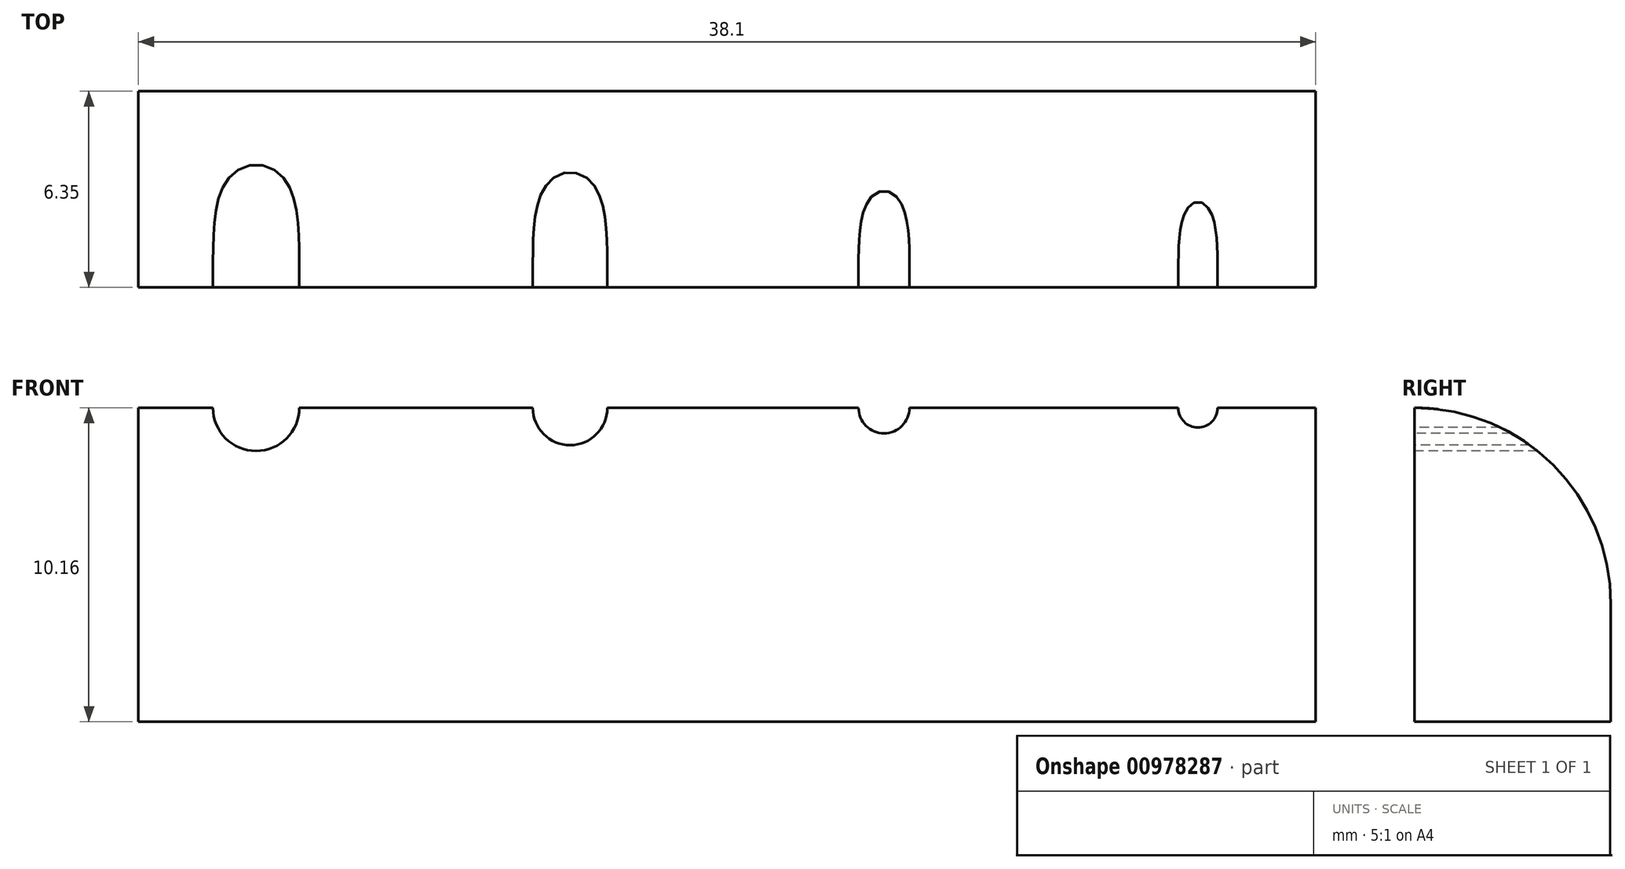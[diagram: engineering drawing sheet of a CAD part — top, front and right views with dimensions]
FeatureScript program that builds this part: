
annotation { "Feature Type Name" : "Feature", "Feature Type Description" : "" }
export const myFeature = defineFeature(function(context is Context, id is Id, definition is map)
    precondition{}
    {
        {
            var Q0;
            Q0=qCreatedBy(makeId("Top.planeOp"),FACE);
            var sketch = newSketch(context, id + "F0", { "sketchPlane" : qUnion([Q0])});
            skLineSegment(sketch, "E0.bottom", {"start": v(-19.05, 0) * mm, "end": v(19.05, 0) * mm});
            skLineSegment(sketch, "E0.top", {"start": v(-19.05, 6.35) * mm, "end": v(19.05, 6.35) * mm});
            skLineSegment(sketch, "E0.left", {"start": v(-19.05, 0) * mm, "end": v(-19.05, 6.35) * mm});
            skLineSegment(sketch, "E0.right", {"start": v(19.05, 0) * mm, "end": v(19.05, 6.35) * mm});
            skSolve(sketch);
        }
        {
            var Q0;
            Q0=makeQuery(id+"F0.imprint","IMPRINT",FACE,{"disambiguationData":[TD([[makeQuery(id+"F0.imprint","IMPRINT",EDGE,{"derivedFrom":sQuery(id+"F0.wireOp",EDGE,"E0.bottom")}),1.0]])]});
            extrude(context, id + "F1", {"entities" : qUnion([Q0]), "depth" : 10.16 * mm, "offsetDistance" : 25.4 * mm});
        }
        {
            var Q0;
            Q0=makeQuery(id+"F1.opExtrude","CAP_EDGE",EDGE,{"disambiguationData":[OSD([sQuery(id+"F0.wireOp",EDGE,"E0.top")])],"isStart":false});
            fillet(context, id + "F2", {"entities" : qUnion([Q0]), "tangentPropagation" : true, "radius" : 6.35 * mm, "defaultsChanged" : true, "vertexSettings" : [], "allowEdgeOverflow" : false});
        }
        {
            var Q0;
            Q0=makeQuery(id+"F1.opExtrude","SWEPT_FACE",FACE,{"disambiguationData":[OSD([sQuery(id+"F0.wireOp",EDGE,"E0.bottom")])]});
            var sketch = newSketch(context, id + "F3", { "sketchPlane" : qUnion([Q0])});
            skCircle(sketch, "E1", {"center": v(-15.24, 10.16) * mm, "radius": 1.4 * mm});
            skCircle(sketch, "E2", {"center": v(-5.08, 10.16) * mm, "radius": 1.2 * mm});
            skCircle(sketch, "E3", {"center": v(5.08, 10.16) * mm, "radius": 0.83 * mm});
            skCircle(sketch, "E4", {"center": v(15.24, 10.16) * mm, "radius": 0.64 * mm});
            skSolve(sketch);
        }
        {
            var Q0;
            {var subQ0=sQuery(id+"F3.wireOp",EDGE,"E1");var subQ1=makeQuery(id+"F2.opFillet","BLEND_EDGE",EDGE,{"blendedFrom":[makeQuery(id+"F1.opExtrude","CAP_EDGE",EDGE,{"disambiguationData":[OSD([sQuery(id+"F0.wireOp",EDGE,"E0.top")])],"isStart":false}),makeQuery(id+"F1.opExtrude","SWEPT_FACE",FACE,{"disambiguationData":[OSD([sQuery(id+"F0.wireOp",EDGE,"E0.bottom")])]})],"blendedInto":[makeQuery(id+"F1.opExtrude","SWEPT_FACE",FACE,{"disambiguationData":[OSD([sQuery(id+"F0.wireOp",EDGE,"E0.bottom")])]})]});var subQ2=makeQuery(id+"F3.imprint","INTERSECT",VERTEX,{"disambiguationData":[OD(0.0)],"derivedFrom":[subQ1,subQ0]});Q0=makeQuery(id+"F3.imprint","IMPRINT",FACE,{"disambiguationData":[TD([[makeQuery(id+"F3.imprint","IMPRINT",EDGE,{"disambiguationData":[TD([[subQ2,-1.0]])],"derivedFrom":subQ0}),1.0]])]});}
            var Q1;
            {var subQ0=sQuery(id+"F3.wireOp",EDGE,"E2");var subQ1=makeQuery(id+"F2.opFillet","BLEND_EDGE",EDGE,{"blendedFrom":[makeQuery(id+"F1.opExtrude","CAP_EDGE",EDGE,{"disambiguationData":[OSD([sQuery(id+"F0.wireOp",EDGE,"E0.top")])],"isStart":false}),makeQuery(id+"F1.opExtrude","SWEPT_FACE",FACE,{"disambiguationData":[OSD([sQuery(id+"F0.wireOp",EDGE,"E0.bottom")])]})],"blendedInto":[makeQuery(id+"F1.opExtrude","SWEPT_FACE",FACE,{"disambiguationData":[OSD([sQuery(id+"F0.wireOp",EDGE,"E0.bottom")])]})]});var subQ2=makeQuery(id+"F3.imprint","INTERSECT",VERTEX,{"disambiguationData":[OD(0.0)],"derivedFrom":[subQ1,subQ0]});Q1=makeQuery(id+"F3.imprint","IMPRINT",FACE,{"disambiguationData":[TD([[makeQuery(id+"F3.imprint","IMPRINT",EDGE,{"disambiguationData":[TD([[subQ2,-1.0]])],"derivedFrom":subQ0}),1.0]])]});}
            var Q2;
            {var subQ0=sQuery(id+"F3.wireOp",EDGE,"E3");var subQ1=makeQuery(id+"F2.opFillet","BLEND_EDGE",EDGE,{"blendedFrom":[makeQuery(id+"F1.opExtrude","CAP_EDGE",EDGE,{"disambiguationData":[OSD([sQuery(id+"F0.wireOp",EDGE,"E0.top")])],"isStart":false}),makeQuery(id+"F1.opExtrude","SWEPT_FACE",FACE,{"disambiguationData":[OSD([sQuery(id+"F0.wireOp",EDGE,"E0.bottom")])]})],"blendedInto":[makeQuery(id+"F1.opExtrude","SWEPT_FACE",FACE,{"disambiguationData":[OSD([sQuery(id+"F0.wireOp",EDGE,"E0.bottom")])]})]});var subQ2=makeQuery(id+"F3.imprint","INTERSECT",VERTEX,{"disambiguationData":[OD(0.0)],"derivedFrom":[subQ1,subQ0]});Q2=makeQuery(id+"F3.imprint","IMPRINT",FACE,{"disambiguationData":[TD([[makeQuery(id+"F3.imprint","IMPRINT",EDGE,{"disambiguationData":[TD([[subQ2,1.0]])],"derivedFrom":subQ0}),1.0]])]});}
            var Q3;
            {var subQ0=sQuery(id+"F3.wireOp",EDGE,"E4");var subQ1=makeQuery(id+"F2.opFillet","BLEND_EDGE",EDGE,{"blendedFrom":[makeQuery(id+"F1.opExtrude","CAP_EDGE",EDGE,{"disambiguationData":[OSD([sQuery(id+"F0.wireOp",EDGE,"E0.top")])],"isStart":false}),makeQuery(id+"F1.opExtrude","SWEPT_FACE",FACE,{"disambiguationData":[OSD([sQuery(id+"F0.wireOp",EDGE,"E0.bottom")])]})],"blendedInto":[makeQuery(id+"F1.opExtrude","SWEPT_FACE",FACE,{"disambiguationData":[OSD([sQuery(id+"F0.wireOp",EDGE,"E0.bottom")])]})]});var subQ2=makeQuery(id+"F3.imprint","INTERSECT",VERTEX,{"disambiguationData":[OD(0.0)],"derivedFrom":[subQ1,subQ0]});Q3=makeQuery(id+"F3.imprint","IMPRINT",FACE,{"disambiguationData":[TD([[makeQuery(id+"F3.imprint","IMPRINT",EDGE,{"disambiguationData":[TD([[subQ2,1.0]])],"derivedFrom":subQ0}),1.0]])]});}
            extrude(context, id + "F4", {"entities" : qUnion([Q0, Q1, Q2, Q3]), "operationType" : NewBodyOperationType.REMOVE, "oppositeDirection" : true, "depth" : 25.4 * mm, "offsetDistance" : 25.4 * mm});
        }
    });
